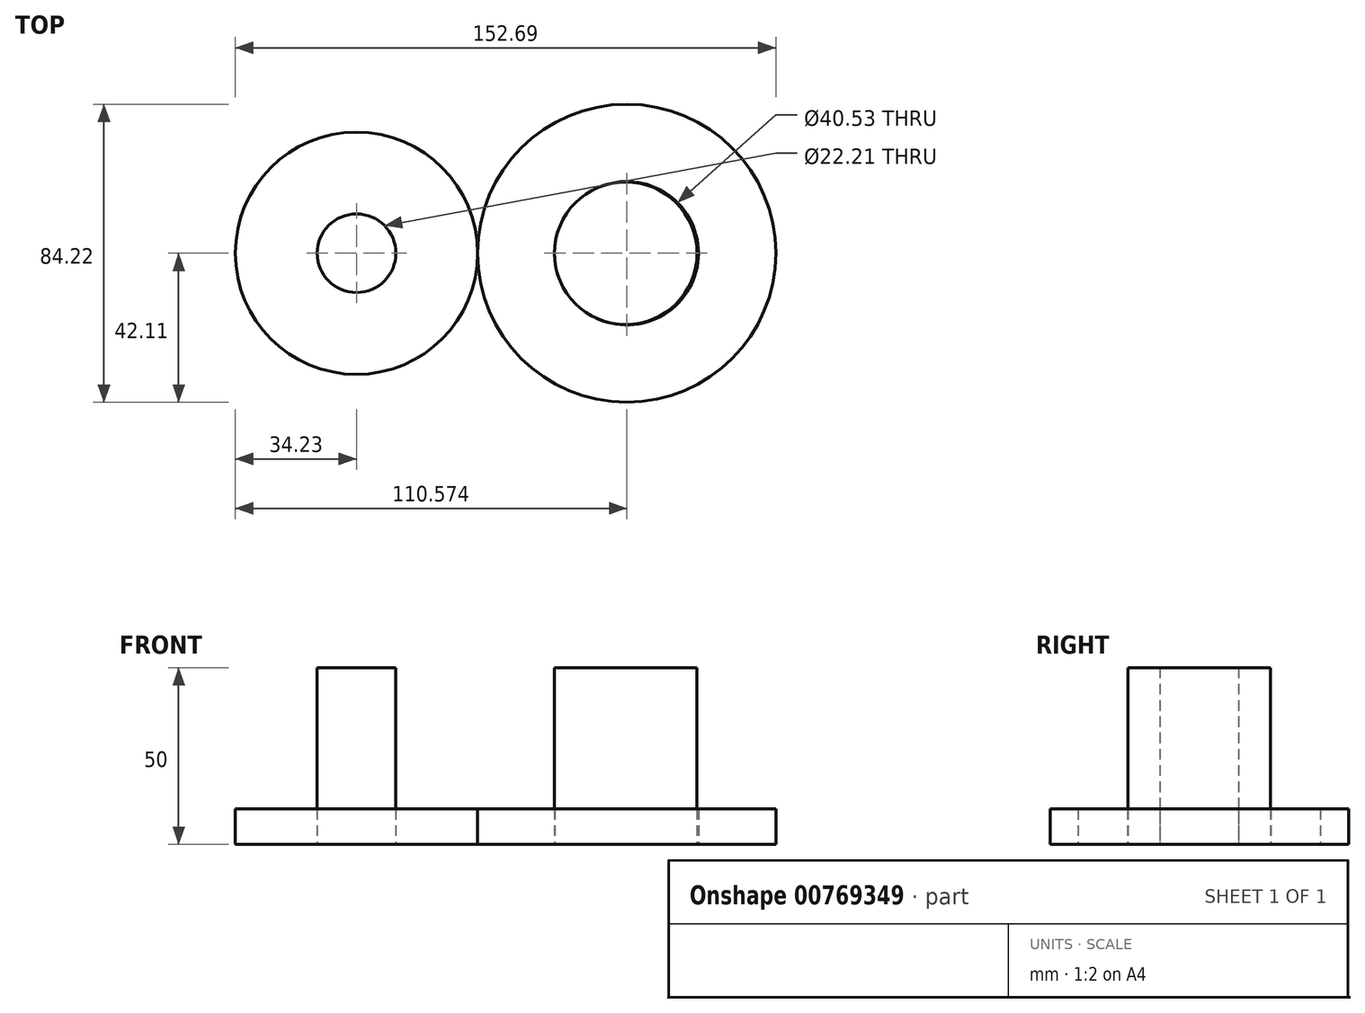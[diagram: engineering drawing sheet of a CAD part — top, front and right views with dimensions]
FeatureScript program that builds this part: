
annotation { "Feature Type Name" : "Feature", "Feature Type Description" : "" }
export const myFeature = defineFeature(function(context is Context, id is Id, definition is map)
    precondition{}
    {
        {
            var Q0;
            Q0=qCreatedBy(makeId("Top.planeOp"),FACE);
            var sketch = newSketch(context, id + "F0", { "sketchPlane" : qUnion([Q0])});
            skCircle(sketch, "E0", {"center": v(0, 0) * mm, "radius": 34.23 * mm});
            skLineSegment(sketch, "E1", {"start": v(0, 0) * mm, "end": v(34.23, 0) * mm});
            skPoint(sketch, "E2", {"position": v(34.23, 0) * mm});
            skCircle(sketch, "E3", {"center": v(76.34, 0) * mm, "radius": 42.11 * mm});
            skPoint(sketch, "E4.1.0", {"position": v(39.33, 36.83) * mm});
            skPoint(sketch, "E4.2.0", {"position": v(92.8, 43.5) * mm});
            skPoint(sketch, "E4.3.0", {"position": v(139.99, 17.48) * mm});
            skPoint(sketch, "E4.4.0", {"position": v(162.86, -31.3) * mm});
            skPoint(sketch, "E4.5.0", {"position": v(152.69, -84.23) * mm});
            skPoint(sketch, "E4.center", {"position": v(76.34, -42.11) * mm});
            skLineSegment(sketch, "E4.anchor1", {"start": v(76.34, -42.11) * mm, "end": v(0, 0) * mm, "construction": true});
            skLineSegment(sketch, "E4.anchor2", {"start": v(76.34, -42.11) * mm, "end": v(152.69, -84.23) * mm, "construction": true});
            skLineSegment(sketch, "E5", {"start": v(76.34, 0) * mm, "end": v(39.33, 36.83) * mm});
            skLineSegment(sketch, "E6", {"start": v(76.34, 0) * mm, "end": v(92.8, 43.5) * mm});
            skLineSegment(sketch, "E7", {"start": v(139.99, 17.48) * mm, "end": v(76.34, 0) * mm});
            skLineSegment(sketch, "E8", {"start": v(162.86, -31.3) * mm, "end": v(76.34, 0) * mm});
            skLineSegment(sketch, "E9", {"start": v(152.69, -84.23) * mm, "end": v(76.34, 0) * mm});
            skLineSegment(sketch, "E10", {"start": v(76.34, -42.11) * mm, "end": v(76.34, 0) * mm});
            skLineSegment(sketch, "E11", {"start": v(34.23, 0) * mm, "end": v(76.34, 0) * mm});
            skCircle(sketch, "E12", {"center": v(76.34, 0) * mm, "radius": 20.27 * mm});
            skCircle(sketch, "E13", {"center": v(0, 0) * mm, "radius": 11.1 * mm});
            skSolve(sketch);
        }
        {
            var Q0;
            Q0=makeQuery(id+"F0.imprint","IMPRINT",FACE,{"disambiguationData":[TD([[makeQuery(id+"F0.imprint","IMPRINT",EDGE,{"derivedFrom":sQuery(id+"F0.wireOp",EDGE,"E0")}),1.0]])]});
            var Q1;
            Q1 = qSketchRegion(id + "F0", true);
            extrude(context, id + "F1", {"entities" : qUnion([Q0, Q1]), "depth" : 10 * mm, "offsetDistance" : 25.4 * mm});
        }
        {
            var Q0;
            Q0=qCreatedBy(makeId("Top.planeOp"),FACE);
            var sketch = newSketch(context, id + "F2", { "sketchPlane" : qUnion([Q0])});
            skPoint(sketch, "E14", {"position": v(11.12, 0) * mm});
            skPoint(sketch, "E15", {"position": v(0, 0) * mm});
            skPoint(sketch, "E16", {"position": v(76.07, 0) * mm});
            skCircle(sketch, "E17", {"center": v(0, 0) * mm, "radius": 11.12 * mm});
            skCircle(sketch, "E18", {"center": v(76.07, 0) * mm, "radius": 20.14 * mm});
            skSolve(sketch);
        }
        {
            var Q0;
            Q0 = qSketchRegion(id + "F2", true);
            extrude(context, id + "F3", {"entities" : qUnion([Q0]), "depth" : 50 * mm, "offsetDistance" : 25.4 * mm});
        }
    });
